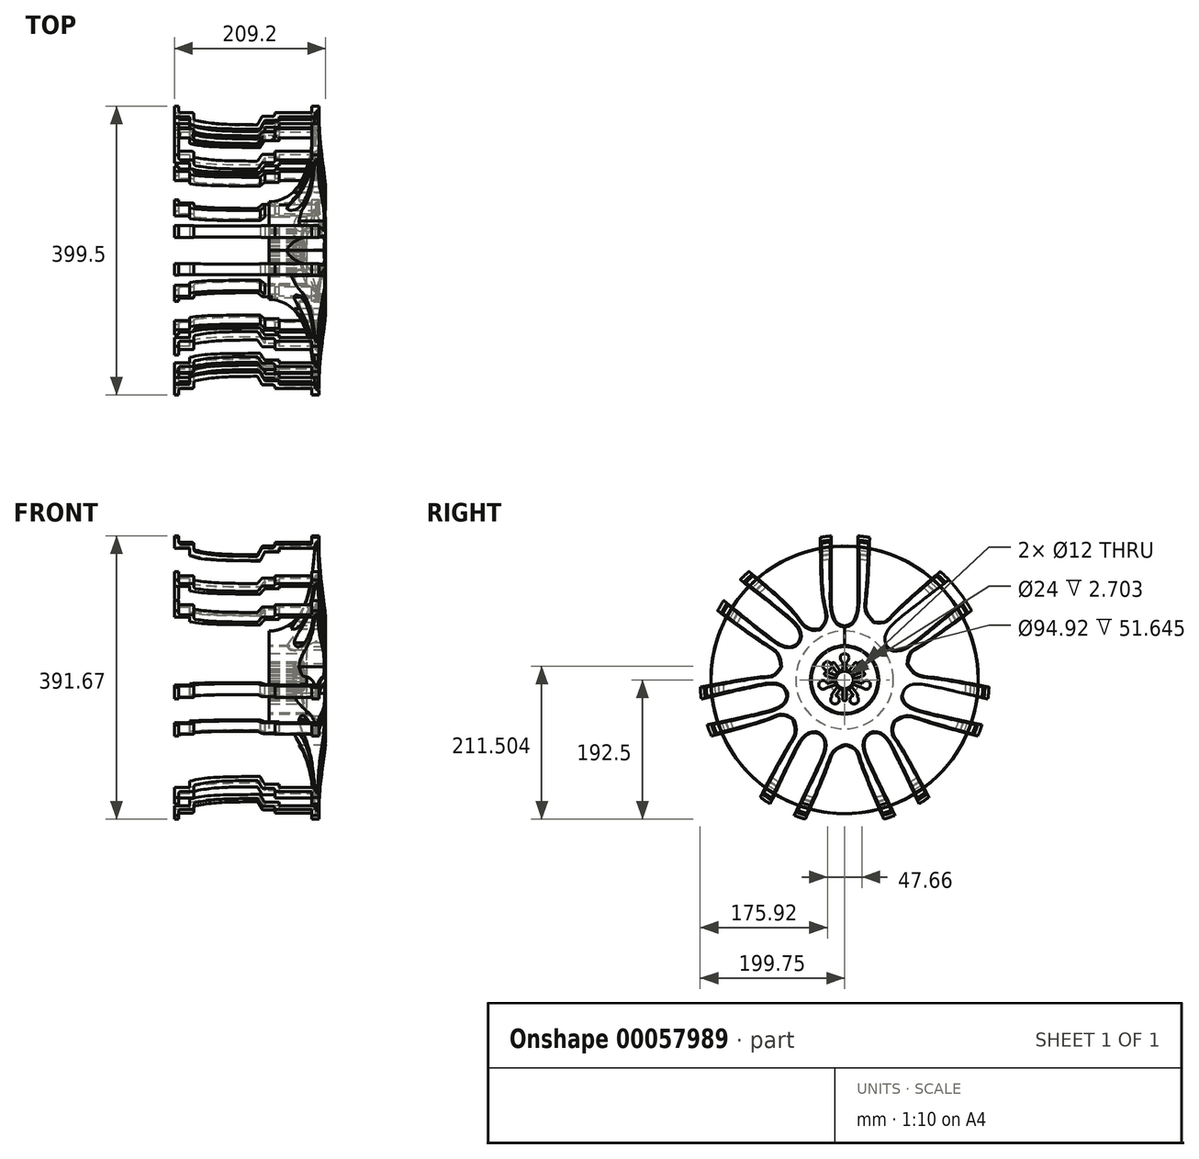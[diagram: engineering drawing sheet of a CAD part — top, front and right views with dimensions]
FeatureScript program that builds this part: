
annotation { "Feature Type Name" : "Feature", "Feature Type Description" : "" }
export const myFeature = defineFeature(function(context is Context, id is Id, definition is map)
    precondition{}
    {
        {
            var Q0;
            Q0=qCreatedBy(makeId("Front.planeOp"),FACE);
            var sketch = newSketch(context, id + "F0", { "sketchPlane" : qUnion([Q0])});
            skLineSegment(sketch, "E0", {"start": v(-200, 200) * mm, "end": v(0, 200) * mm, "construction": true});
            skLineSegment(sketch, "E1", {"start": v(0, 200) * mm, "end": v(0, 0) * mm, "construction": true});
            skLineSegment(sketch, "E2", {"start": v(0, 0) * mm, "end": v(-200, 0) * mm, "construction": true});
            skLineSegment(sketch, "E3", {"start": v(-200, 0) * mm, "end": v(-200, 200) * mm, "construction": true});
            skLineSegment(sketch, "E4", {"start": v(-200, 168) * mm, "end": v(0, 168) * mm, "construction": true});
            skLineSegment(sketch, "E5", {"start": v(0, 200) * mm, "end": v(0, 185) * mm});
            skLineSegment(sketch, "E6", {"start": v(0, 185) * mm, "end": v(-55, 185) * mm});
            skLineSegment(sketch, "E7", {"start": v(-55, 185) * mm, "end": v(-55, 180) * mm});
            skLineSegment(sketch, "E8", {"start": v(-55, 180) * mm, "end": v(-75, 180) * mm});
            skLineSegment(sketch, "E9", {"start": v(-200, 200) * mm, "end": v(-200, 185) * mm});
            skLineSegment(sketch, "E10", {"start": v(-200, 185) * mm, "end": v(-178.8, 185) * mm});
            skLineSegment(sketch, "E11", {"start": v(-178.8, 185) * mm, "end": v(-178.8, 175) * mm});
            skLineSegment(sketch, "E12", {"start": v(-75, 180) * mm, "end": v(-81.33, 168) * mm});
            skFitSpline(sketch, "E13", {"points": [v(-178.8, 175) * mm, v(-81.33, 168) * mm], "startDerivative": vector(39.43, -8.88) * mm, "endDerivative": vector(260.91, 0) * mm});
            skLineSegment(sketch, "E14", {"start": v(-200, 200) * mm, "end": v(-194, 200) * mm});
            skLineSegment(sketch, "E15", {"start": v(-194, 200) * mm, "end": v(-194, 191) * mm});
            skLineSegment(sketch, "E16", {"start": v(-194, 191) * mm, "end": v(-172.81, 191) * mm});
            skLineSegment(sketch, "E17", {"start": v(0, 200) * mm, "end": v(-10, 200) * mm});
            skLineSegment(sketch, "E18", {"start": v(-10, 200) * mm, "end": v(-10, 191) * mm});
            skLineSegment(sketch, "E19", {"start": v(-10, 191) * mm, "end": v(-61, 191) * mm});
            skLineSegment(sketch, "E20", {"start": v(-61, 191) * mm, "end": v(-61, 186) * mm});
            skLineSegment(sketch, "E21", {"start": v(-61, 186) * mm, "end": v(-78.62, 186) * mm});
            skLineSegment(sketch, "E22", {"start": v(-78.62, 186) * mm, "end": v(-84.94, 174) * mm});
            skLineSegment(sketch, "E23", {"start": v(-172.81, 191) * mm, "end": v(-172.81, 181) * mm});
            skFitSpline(sketch, "E24", {"points": [v(-172.81, 181) * mm, v(-84.94, 174) * mm], "startDerivative": vector(84.8, -22.47) * mm, "endDerivative": vector(95.11, -2) * mm});
            skSolve(sketch);
        }
        {
            var Q0;
            Q0=qSketchRegion(id+"F0",true);
            var Q1;
            Q1=sQuery(id+"F0.wireOp",EDGE,"E2");
            revolve(context, id + "F1", {"entities" : qUnion([Q0]), "axis" : qUnion([Q1]), "revolveType" : RevolveType.FULL});
        }
        {
            var Q0;
            Q0=makeQuery(id+"F1.opRevolve","SWEPT_EDGE",EDGE,{"disambiguationData":[OSD([sQuery(id+"F0.wireOp",EDGE,"E16"),sQuery(id+"F0.wireOp",EDGE,"E23")])]});
            fillet(context, id + "F2", {"entities" : qUnion([Q0]), "radius" : 3 * mm, "tangentPropagation" : true, "allowEdgeOverflow" : false});
        }
        {
            var Q0;
            Q0=makeQuery(id+"F1.opRevolve","SWEPT_EDGE",EDGE,{"disambiguationData":[OSD([sQuery(id+"F0.wireOp",EDGE,"E15"),sQuery(id+"F0.wireOp",EDGE,"E16")])]});
            fillet(context, id + "F3", {"entities" : qUnion([Q0]), "radius" : 3 * mm, "tangentPropagation" : true, "allowEdgeOverflow" : false});
        }
        {
            var Q0;
            Q0=makeQuery(id+"F1.opRevolve","SWEPT_EDGE",EDGE,{"disambiguationData":[OSD([sQuery(id+"F0.wireOp",EDGE,"E23"),sQuery(id+"F0.wireOp",EDGE,"E24")])]});
            fillet(context, id + "F4", {"entities" : qUnion([Q0]), "radius" : 3 * mm, "tangentPropagation" : true, "allowEdgeOverflow" : false});
        }
        {
            var Q0;
            Q0=makeQuery(id+"F1.opRevolve","SWEPT_EDGE",EDGE,{"disambiguationData":[OSD([sQuery(id+"F0.wireOp",EDGE,"E22"),sQuery(id+"F0.wireOp",EDGE,"E24")])]});
            fillet(context, id + "F5", {"entities" : qUnion([Q0]), "radius" : 3 * mm, "tangentPropagation" : true, "allowEdgeOverflow" : false});
        }
        {
            var Q0;
            Q0=makeQuery(id+"F1.opRevolve","SWEPT_EDGE",EDGE,{"disambiguationData":[OSD([sQuery(id+"F0.wireOp",EDGE,"E21"),sQuery(id+"F0.wireOp",EDGE,"E22")])]});
            fillet(context, id + "F6", {"entities" : qUnion([Q0]), "radius" : 3 * mm, "tangentPropagation" : true, "allowEdgeOverflow" : false});
        }
        {
            var Q0;
            Q0=makeQuery(id+"F1.opRevolve","SWEPT_EDGE",EDGE,{"disambiguationData":[OSD([sQuery(id+"F0.wireOp",EDGE,"E20"),sQuery(id+"F0.wireOp",EDGE,"E21")])]});
            fillet(context, id + "F7", {"entities" : qUnion([Q0]), "radius" : 3 * mm, "tangentPropagation" : true, "allowEdgeOverflow" : false});
        }
        {
            var Q0;
            Q0=makeQuery(id+"F1.opRevolve","SWEPT_FACE",FACE,{"disambiguationData":[OSD([sQuery(id+"F0.wireOp",EDGE,"E5")])]});
            var sketch = newSketch(context, id + "F8", { "sketchPlane" : qUnion([Q0])});
            skArc(sketch, "E25", {"start": v(82.65, 71.65) * mm, "mid": v(-145.3, -223.22) * mm, "end": v(182.84, -46.5) * mm});
            skArc(sketch, "E26", {"start": v(179.13, -35.13) * mm, "mid": v(109.4, 55.97) * mm, "end": v(0, 90.5) * mm});
            skLineSegment(sketch, "E27", {"start": v(179.13, -35.13) * mm, "end": v(122.22, 138.87) * mm});
            skArc(sketch, "E28.MirrorCS", {"start": v(80.26, 66.69) * mm, "mid": v(87.85, 62.8) * mm, "end": v(95.26, 58.59) * mm});
            skLineSegment(sketch, "E29.MirrorCS", {"start": v(95.26, 58.59) * mm, "end": v(106.47, 62.77) * mm});
            skArc(sketch, "E30.MirrorCS", {"start": v(106.47, 62.77) * mm, "mid": v(130.91, 43.85) * mm, "end": v(152.05, 21.3) * mm});
            skArc(sketch, "E31.1.0", {"start": v(60.97, 80.5) * mm, "mid": v(-53.73, 82.77) * mm, "end": v(-148.95, 18.78) * mm});
            skLineSegment(sketch, "E31.1.1", {"start": v(60.97, 80.5) * mm, "end": v(-110.55, 144.5) * mm});
            skArc(sketch, "E31.1.2", {"start": v(-82.67, 71.64) * mm, "mid": v(5.75, -290.42) * mm, "end": v(72.17, 76.3) * mm});
            skArc(sketch, "E31.1.3", {"start": v(-80.28, 66.67) * mm, "mid": v(-72.52, 70.2) * mm, "end": v(-64.6, 73.36) * mm});
            skArc(sketch, "E31.1.4", {"start": v(-60.88, 84.73) * mm, "mid": v(-30.84, 92.04) * mm, "end": v(-0.03, 94.5) * mm});
            skLineSegment(sketch, "E31.1.5", {"start": v(-64.6, 73.36) * mm, "end": v(-60.88, 84.73) * mm});
            skArc(sketch, "E31.2.0", {"start": v(-103.1, 60.2) * mm, "mid": v(-176.4, -28.05) * mm, "end": v(-185.73, -142.4) * mm});
            skLineSegment(sketch, "E31.2.1", {"start": v(-103.1, 60.2) * mm, "end": v(-260.08, -34) * mm});
            skArc(sketch, "E31.2.2", {"start": v(-185.74, -57.62) * mm, "mid": v(152.46, -214.24) * mm, "end": v(-92.84, 66.35) * mm});
            skArc(sketch, "E31.2.3", {"start": v(-180.36, -58.85) * mm, "mid": v(-178.28, -50.58) * mm, "end": v(-175.8, -42.42) * mm});
            skArc(sketch, "E31.2.4", {"start": v(-182.38, -32.42) * mm, "mid": v(-169.37, -4.38) * mm, "end": v(-152.08, 21.25) * mm});
            skLineSegment(sketch, "E31.2.5", {"start": v(-175.8, -42.42) * mm, "end": v(-182.38, -32.42) * mm});
            skArc(sketch, "E31.3.0", {"start": v(-189.53, -80.72) * mm, "mid": v(-166.24, -193.06) * mm, "end": v(-82.66, -271.64) * mm});
            skLineSegment(sketch, "E31.3.1", {"start": v(-189.53, -80.72) * mm, "end": v(-213.76, -262.19) * mm});
            skArc(sketch, "E31.3.2", {"start": v(-148.94, -218.8) * mm, "mid": v(184.37, -52.03) * mm, "end": v(-187.95, -68.87) * mm});
            skArc(sketch, "E31.3.3", {"start": v(-144.63, -215.36) * mm, "mid": v(-149.8, -208.57) * mm, "end": v(-154.64, -201.55) * mm});
            skArc(sketch, "E31.3.4", {"start": v(-166.55, -200.46) * mm, "mid": v(-180.36, -172.8) * mm, "end": v(-189.62, -143.3) * mm});
            skLineSegment(sketch, "E31.3.5", {"start": v(-154.64, -201.55) * mm, "end": v(-166.55, -200.46) * mm});
            skArc(sketch, "E31.4.0", {"start": v(-133.24, -236.16) * mm, "mid": v(-30.9, -287.99) * mm, "end": v(82.66, -271.64) * mm});
            skLineSegment(sketch, "E31.4.1", {"start": v(-133.24, -236.16) * mm, "end": v(-6.48, -368.25) * mm});
            skArc(sketch, "E31.4.2", {"start": v(0.01, -290.5) * mm, "mid": v(77.45, 74.06) * mm, "end": v(-141.52, -227.53) * mm});
            skArc(sketch, "E31.4.3", {"start": v(0.01, -285) * mm, "mid": v(-8.51, -284.8) * mm, "end": v(-17.02, -284.22) * mm});
            skArc(sketch, "E31.4.4", {"start": v(-25.3, -292.85) * mm, "mid": v(-55.53, -286.4) * mm, "end": v(-84.36, -275.25) * mm});
            skLineSegment(sketch, "E31.4.5", {"start": v(-17.02, -284.22) * mm, "end": v(-25.3, -292.85) * mm});
            skArc(sketch, "E31.5.0", {"start": v(23.38, -289.07) * mm, "mid": v(127.71, -241.36) * mm, "end": v(185.73, -142.4) * mm});
            skLineSegment(sketch, "E31.5.1", {"start": v(23.38, -289.07) * mm, "end": v(205.69, -272.31) * mm});
            skArc(sketch, "E31.5.2", {"start": v(148.95, -218.77) * mm, "mid": v(-87.8, 69.07) * mm, "end": v(11.47, -290.16) * mm});
            skArc(sketch, "E31.5.3", {"start": v(144.65, -215.33) * mm, "mid": v(139.18, -221.88) * mm, "end": v(133.41, -228.16) * mm});
            skArc(sketch, "E31.5.4", {"start": v(135, -240.02) * mm, "mid": v(111.11, -259.64) * mm, "end": v(84.42, -275.23) * mm});
            skLineSegment(sketch, "E31.5.5", {"start": v(133.41, -228.16) * mm, "end": v(135, -240.02) * mm});
            skArc(sketch, "E31.6.0", {"start": v(162.4, -199.6) * mm, "mid": v(190.15, -88.29) * mm, "end": v(148.95, 18.78) * mm});
            skLineSegment(sketch, "E31.6.1", {"start": v(162.4, -199.6) * mm, "end": v(262.97, -46.62) * mm});
            skArc(sketch, "E31.6.2", {"start": v(185.73, -57.6) * mm, "mid": v(-186.93, -63.23) * mm, "end": v(155.83, -209.6) * mm});
            skArc(sketch, "E31.6.3", {"start": v(180.36, -58.82) * mm, "mid": v(182.06, -67.18) * mm, "end": v(183.38, -75.6) * mm});
            skArc(sketch, "E31.6.4", {"start": v(193.64, -81.75) * mm, "mid": v(194.09, -112.66) * mm, "end": v(189.63, -143.25) * mm});
            skLineSegment(sketch, "E31.6.5", {"start": v(183.38, -75.6) * mm, "end": v(193.64, -81.75) * mm});
            skSolve(sketch);
        }
        {
            var Q0;
            {var subQ0=sQuery(id+"F0.wireOp",EDGE,"E5");Q0=makeQuery(id+"F8.imprint","IMPRINT",FACE,{"disambiguationData":[TD([[makeQuery(id+"F8.imprint","IMPRINT",EDGE,{"derivedFrom":makeQuery(id+"F1.opRevolve","SWEPT_EDGE",EDGE,{"disambiguationData":[OSD([subQ0,sQuery(id+"F0.wireOp",EDGE,"E17")])]})}),1.0]])]});}
            cPlane(context, id + "F9", {"entities" : qUnion([Q0]), "cplaneType" : CPlaneType.OFFSET, "offset" : 2 * mm, "width" : 152.4 * mm, "height" : 152.4 * mm});
        }
        {
            var Q0;
            Q0=qCreatedBy(id+"F9.planeOp",FACE);
            var sketch = newSketch(context, id + "F10", { "sketchPlane" : qUnion([Q0])});
            skArc(sketch, "E32", {"start": v(-193.59, 18.53) * mm, "mid": v(-189.67, -43.35) * mm, "end": v(-166.47, -100.86) * mm});
            skArc(sketch, "E33", {"start": v(175.53, 57.28) * mm, "mid": v(144.15, 115.24) * mm, "end": v(94.42, 158.5) * mm});
            skLineSegment(sketch, "E34", {"start": v(-182.24, 67.68) * mm, "end": v(-175.61, 57.03) * mm});
            skLineSegment(sketch, "E35", {"start": v(-106.28, 162.62) * mm, "end": v(-94.48, 158.46) * mm});
            skLineSegment(sketch, "E36", {"start": v(-65.52, 172.44) * mm, "end": v(-61.02, 184.4) * mm});
            skLineSegment(sketch, "E37", {"start": v(-193.59, 18.53) * mm, "end": v(-183.05, 24.59) * mm});
            skLineSegment(sketch, "E38", {"start": v(-166.47, -100.86) * mm, "end": v(-153.9, -102.44) * mm});
            skLineSegment(sketch, "E39", {"start": v(-135.3, -140) * mm, "end": v(-133.44, -128.02) * mm});
            skLineSegment(sketch, "E40", {"start": v(-25.44, -193.1) * mm, "end": v(-16.16, -184.3) * mm});
            skLineSegment(sketch, "E41", {"start": v(25.42, -193.1) * mm, "end": v(16.48, -184.26) * mm});
            skLineSegment(sketch, "E42", {"start": v(134.96, -140.33) * mm, "end": v(132.99, -128.48) * mm});
            skLineSegment(sketch, "E43", {"start": v(166.75, -100.4) * mm, "end": v(154, -102.28) * mm});
            skLineSegment(sketch, "E44", {"start": v(193.66, 17.73) * mm, "end": v(183.08, 24.35) * mm});
            skLineSegment(sketch, "E45", {"start": v(175.53, 57.28) * mm, "end": v(182.24, 67.7) * mm});
            skLineSegment(sketch, "E46", {"start": v(64.54, 172.8) * mm, "end": v(60.48, 184.58) * mm});
            skLineSegment(sketch, "E47", {"start": v(94.42, 158.5) * mm, "end": v(106.43, 162.52) * mm});
            skArc(sketch, "E48.trimOffspring", {"start": v(-106.28, 162.62) * mm, "mid": v(-151.87, 121.24) * mm, "end": v(-182.24, 67.68) * mm});
            skArc(sketch, "E49.trimOffspring", {"start": v(60.48, 184.58) * mm, "mid": v(-0.28, 194.23) * mm, "end": v(-61.02, 184.4) * mm});
            skArc(sketch, "E50.trimOffspring", {"start": v(-135.3, -140) * mm, "mid": v(-84.64, -175.4) * mm, "end": v(-25.44, -193.1) * mm});
            skArc(sketch, "E51.trimOffspring", {"start": v(25.42, -193.1) * mm, "mid": v(84.42, -175.5) * mm, "end": v(134.96, -140.33) * mm});
            skArc(sketch, "E52.trimOffspring", {"start": v(166.75, -100.4) * mm, "mid": v(189.64, -43.48) * mm, "end": v(193.66, 17.73) * mm});
            skArc(sketch, "E53.trimOffspring", {"start": v(182.24, 67.7) * mm, "mid": v(151.92, 121.17) * mm, "end": v(106.43, 162.52) * mm});
            skArc(sketch, "E54.trimOffspring", {"start": v(154, -102.28) * mm, "mid": v(180.04, -41.6) * mm, "end": v(183.08, 24.35) * mm});
            skArc(sketch, "E55.trimOffspring", {"start": v(16.48, -184.26) * mm, "mid": v(79.77, -166.89) * mm, "end": v(132.99, -128.48) * mm});
            skArc(sketch, "E56.trimOffspring", {"start": v(-133.44, -128.02) * mm, "mid": v(-79.92, -166.82) * mm, "end": v(-16.16, -184.3) * mm});
            skArc(sketch, "E57.trimOffspring", {"start": v(-183.05, 24.59) * mm, "mid": v(-180.05, -41.58) * mm, "end": v(-153.9, -102.44) * mm});
            skArc(sketch, "E58.trimOffspring", {"start": v(-94.48, 158.46) * mm, "mid": v(-144.25, 115.12) * mm, "end": v(-175.61, 57.03) * mm});
            skArc(sketch, "E59.trimOffspring", {"start": v(64.54, 172.8) * mm, "mid": v(-0.52, 184.45) * mm, "end": v(-65.52, 172.44) * mm});
            skSolve(sketch);
        }
        {
            var Q0;
            Q0=qSketchRegion(id+"F10",true);
            extrude(context, id + "F11", {"entities" : qUnion([Q0]), "operationType" : NewBodyOperationType.REMOVE, "oppositeDirection" : true, "depth" : 4 * mm});
        }
        {
            var Q0;
            Q0=qCreatedBy(makeId("Front.planeOp"),FACE);
            var sketch = newSketch(context, id + "F12", { "sketchPlane" : qUnion([Q0])});
            skLineSegment(sketch, "E60", {"start": v(0, 191.75) * mm, "end": v(-4.92, 191.75) * mm});
            skLineSegment(sketch, "E61", {"start": v(-17.14, 47.46) * mm, "end": v(-68.78, 47.46) * mm});
            skLineSegment(sketch, "E62", {"start": v(-68.78, 47.46) * mm, "end": v(-68.78, 67.56) * mm});
            skFitSpline(sketch, "E63", {"points": [v(0, 191.75) * mm, v(-17.14, 47.46) * mm], "startDerivative": vector(0, -276.55) * mm, "endDerivative": vector(-139.92, -42.5) * mm});
            skFitSpline(sketch, "E64", {"points": [v(-4.92, 191.75) * mm, v(-68.78, 67.56) * mm], "startDerivative": vector(-14.16, -151.7) * mm, "endDerivative": vector(-167.36, -6.57) * mm});
            skLineSegment(sketch, "E65", {"start": v(-115.73, 0) * mm, "end": v(0, 0) * mm, "construction": true});
            skSolve(sketch);
        }
        {
            var Q0;
            Q0=qCreatedBy(makeId("Front.planeOp"),FACE);
            var sketch = newSketch(context, id + "F13", { "sketchPlane" : qUnion([Q0])});
            skLineSegment(sketch, "E66", {"start": v(0, 0) * mm, "end": v(181.72, 0) * mm, "construction": true});
            skSolve(sketch);
        }
        {
            var Q0;
            Q0=qSketchRegion(id+"F12",true);
            var Q1;
            Q1=sQuery(id+"F12.wireOp",EDGE,"E65");
            revolve(context, id + "F14", {"entities" : qUnion([Q0]), "axis" : qUnion([Q1]), "revolveType" : RevolveType.FULL});
        }
        {
            var Q0;
            Q0=qCreatedBy(makeId("Right.planeOp"),FACE);
            var sketch = newSketch(context, id + "F15", { "sketchPlane" : qUnion([Q0])});
            skFitSpline(sketch, "E67", {"points": [v(18.15, 199.17) * mm, v(18.5, 120.67) * mm, v(0, 74.57) * mm], "startDerivative": vector(4.65, -291.73) * mm, "endDerivative": vector(-131.17, -9.85) * mm});
            skFitSpline(sketch, "E68", {"points": [v(34.66, 196.97) * mm, v(29.92, 109.84) * mm, v(40.85, 80.56) * mm], "startDerivative": vector(-3.25, -176.46) * mm, "endDerivative": vector(105.11, -100.34) * mm});
            skLineSegment(sketch, "E69", {"start": v(0, 200) * mm, "end": v(0, 74.57) * mm});
            skFitSpline(sketch, "E70.MirrorCS", {"points": [v(-18.15, 199.17) * mm, v(-18.5, 120.67) * mm, v(0, 74.57) * mm], "startDerivative": vector(-4.65, -291.73) * mm, "endDerivative": vector(131.17, -9.85) * mm});
            skFitSpline(sketch, "E71.MirrorCS", {"points": [v(-33.77, 197.13) * mm, v(-29, 105.47) * mm, v(-34.74, 70.51) * mm], "startDerivative": vector(4.34, -176.59) * mm, "endDerivative": vector(-104.67, -100.89) * mm});
            skLineSegment(sketch, "E72.1.0", {"start": v(-156.37, 124.7) * mm, "end": v(-58.3, 46.5) * mm, "construction": true});
            skLineSegment(sketch, "E72.3.0", {"start": v(-86.78, -180.2) * mm, "end": v(-32.36, -67.19) * mm, "construction": true});
            skLineSegment(sketch, "E72.4.0", {"start": v(86.78, -180.2) * mm, "end": v(32.36, -67.19) * mm, "construction": true});
            skLineSegment(sketch, "E72.5.0", {"start": v(194.99, -44.5) * mm, "end": v(72.7, -16.6) * mm, "construction": true});
            skLineSegment(sketch, "E72.6.0", {"start": v(156.37, 124.7) * mm, "end": v(58.3, 46.5) * mm, "construction": true});
            skPoint(sketch, "E72.center", {"position": v(0, 0) * mm});
            skFitSpline(sketch, "E73.MirrorCS", {"points": [v(-132.4, 149.9) * mm, v(-65.2, 87.81) * mm, v(-34.74, 70.51) * mm], "startDerivative": vector(138.32, -110.16) * mm, "endDerivative": vector(143.74, 22.07) * mm});
            skFitSpline(sketch, "E74.MirrorCS", {"points": [v(198.24, -26.48) * mm, v(121.76, -8.8) * mm, v(80.37, -18.34) * mm], "startDerivative": vector(-283.38, 69.45) * mm, "endDerivative": vector(-38.79, -125.69) * mm});
            skFitSpline(sketch, "E75.MirrorCS", {"points": [v(198.24, -26.48) * mm, v(121.76, -8.8) * mm, v(80.37, -18.34) * mm], "startDerivative": vector(-283.38, 69.45) * mm, "endDerivative": vector(-38.79, -125.69) * mm});
            skFitSpline(sketch, "E76.MirrorCS", {"points": [v(190.1, -62.15) * mm, v(113.53, -44.9) * mm, v(80.37, -18.34) * mm], "startDerivative": vector(-285.45, 60.38) * mm, "endDerivative": vector(19.59, 130.07) * mm});
            skFitSpline(sketch, "E77.MirrorCS", {"points": [v(132.4, 149.9) * mm, v(64.99, 88.84) * mm, v(40.85, 80.56) * mm], "startDerivative": vector(-133.89, -115.5) * mm, "endDerivative": vector(-144.5, 16.42) * mm});
            skFitSpline(sketch, "E78", {"points": [v(144.18, 138.35) * mm, v(81.98, 90.08) * mm, v(58.3, 46.5) * mm], "startDerivative": vector(-155.93, -120.73) * mm, "endDerivative": vector(65.65, -114.26) * mm});
            skFitSpline(sketch, "E79.MirrorCS", {"points": [v(166.97, 109.78) * mm, v(106.06, 59.88) * mm, v(58.3, 46.5) * mm], "startDerivative": vector(-152.4, -125.16) * mm, "endDerivative": vector(-96.79, 89.43) * mm});
            skFitSpline(sketch, "E80.MirrorCS", {"points": [v(175.6, 95.71) * mm, v(101.08, 43.59) * mm, v(87.63, 21.9) * mm], "startDerivative": vector(-142.4, -104.83) * mm, "endDerivative": vector(-16.14, -144.53) * mm});
            skFitSpline(sketch, "E81.MirrorCS", {"points": [v(199.75, -10.04) * mm, v(113.75, 4.73) * mm, v(87.63, 21.9) * mm], "startDerivative": vector(-172.76, 36.1) * mm, "endDerivative": vector(-74.43, 124.8) * mm});
            skFitSpline(sketch, "E82.MirrorCS", {"points": [v(184.32, -77.62) * mm, v(100.43, -53.62) * mm, v(69.45, -57.75) * mm], "startDerivative": vector(-171.31, 42.43) * mm, "endDerivative": vector(-121.21, -80.15) * mm});
            skFitSpline(sketch, "E83.MirrorCS", {"points": [v(116.69, -162.43) * mm, v(72.16, -83.13) * mm, v(69.45, -57.75) * mm], "startDerivative": vector(-82.8, 156.23) * mm, "endDerivative": vector(48.16, 137.22) * mm});
            skFitSpline(sketch, "E84.MirrorCS", {"points": [v(102.9, -171.5) * mm, v(69.03, -100.69) * mm, v(35.77, -74.28) * mm], "startDerivative": vector(-122.38, 264.86) * mm, "endDerivative": vector(-122.45, -48.04) * mm});
            skFitSpline(sketch, "E85.MirrorCS", {"points": [v(69.93, -187.38) * mm, v(35.68, -116.75) * mm, v(35.77, -74.28) * mm], "startDerivative": vector(-130.77, 260.82) * mm, "endDerivative": vector(113.9, 65.78) * mm});
            skFitSpline(sketch, "E86.MirrorCS", {"points": [v(54.24, -192.5) * mm, v(20, -108.24) * mm, v(1.85, -90.3) * mm], "startDerivative": vector(-70.52, 162.15) * mm, "endDerivative": vector(-137.31, 47.9) * mm});
            skFitSpline(sketch, "E87.MirrorCS", {"points": [v(-54.24, -192.5) * mm, v(-20.7, -111.95) * mm, v(1.85, -90.3) * mm], "startDerivative": vector(73.64, 160.4) * mm, "endDerivative": vector(138.24, 44.8) * mm});
            skFitSpline(sketch, "E88.MirrorCS", {"points": [v(-69.93, -187.38) * mm, v(-35.68, -116.75) * mm, v(-35.77, -74.28) * mm], "startDerivative": vector(130.77, 260.82) * mm, "endDerivative": vector(-113.9, 65.78) * mm});
            skFitSpline(sketch, "E89.MirrorCS", {"points": [v(-102.9, -171.5) * mm, v(-69.03, -100.69) * mm, v(-35.77, -74.28) * mm], "startDerivative": vector(122.38, 264.86) * mm, "endDerivative": vector(122.45, -48.04) * mm});
            skFitSpline(sketch, "E90.MirrorCS", {"points": [v(-116.69, -162.43) * mm, v(-74.62, -85.98) * mm, v(-71.75, -54.86) * mm], "startDerivative": vector(79.49, 157.58) * mm, "endDerivative": vector(-51.17, 136) * mm});
            skFitSpline(sketch, "E91.MirrorCS", {"points": [v(-184.32, -77.62) * mm, v(-97.1, -51.85) * mm, v(-71.75, -54.86) * mm], "startDerivative": vector(170.74, 45.97) * mm, "endDerivative": vector(123.06, -77.49) * mm});
            skFitSpline(sketch, "E92.MirrorCS", {"points": [v(-190.1, -62.15) * mm, v(-113.53, -44.9) * mm, v(-80.37, -18.34) * mm], "startDerivative": vector(285.45, 60.38) * mm, "endDerivative": vector(-19.59, 130.07) * mm});
            skFitSpline(sketch, "E93.MirrorCS", {"points": [v(-198.24, -26.48) * mm, v(-121.76, -8.8) * mm, v(-80.37, -18.34) * mm], "startDerivative": vector(283.38, 69.45) * mm, "endDerivative": vector(38.79, -125.69) * mm});
            skLineSegment(sketch, "E94.MirrorCS", {"start": v(-194.99, -44.5) * mm, "end": v(-72.7, -16.6) * mm, "construction": true});
            skFitSpline(sketch, "E95.MirrorCS", {"points": [v(-199.75, -10.04) * mm, v(-109.98, 4.58) * mm, v(-88.45, 18.3) * mm], "startDerivative": vector(173.78, 32.67) * mm, "endDerivative": vector(77.25, 123.2) * mm});
            skFitSpline(sketch, "E96.MirrorCS", {"points": [v(-175.6, 95.71) * mm, v(-104.53, 45.09) * mm, v(-88.45, 18.3) * mm], "startDerivative": vector(139.98, -107.48) * mm, "endDerivative": vector(12.9, -144.74) * mm});
            skFitSpline(sketch, "E97.MirrorCS", {"points": [v(-167.12, 109.87) * mm, v(-105.88, 60.77) * mm, v(-64.46, 51.4) * mm], "startDerivative": vector(225.18, -185.53) * mm, "endDerivative": vector(89.48, 96.41) * mm});
            skFitSpline(sketch, "E98.MirrorCS", {"points": [v(-144.3, 138.48) * mm, v(-82.8, 89.7) * mm, v(-64.46, 51.4) * mm], "startDerivative": vector(230.98, -178.25) * mm, "endDerivative": vector(-74.08, -108.69) * mm});
            skArc(sketch, "E99", {"start": v(-33.77, 197.13) * mm, "mid": v(-86.37, 180.39) * mm, "end": v(-132.4, 149.9) * mm});
            skArc(sketch, "E100.trimOffspring", {"start": v(18.15, 199.17) * mm, "mid": v(0, 200) * mm, "end": v(-18.15, 199.17) * mm});
            skArc(sketch, "E101.trimOffspring", {"start": v(199.75, -10.04) * mm, "mid": v(194.99, 44.5) * mm, "end": v(175.6, 95.71) * mm});
            skArc(sketch, "E102.trimOffspring", {"start": v(190.1, -62.15) * mm, "mid": v(194.99, -44.5) * mm, "end": v(198.24, -26.48) * mm});
            skArc(sketch, "E103.trimOffspring", {"start": v(116.69, -162.43) * mm, "mid": v(156.37, -124.7) * mm, "end": v(184.32, -77.62) * mm});
            skArc(sketch, "E104.trimOffspring", {"start": v(69.93, -187.38) * mm, "mid": v(86.78, -180.2) * mm, "end": v(102.9, -171.5) * mm});
            skArc(sketch, "E105.trimOffspring", {"start": v(-54.24, -192.5) * mm, "mid": v(0, -200) * mm, "end": v(54.24, -192.5) * mm});
            skArc(sketch, "E106.trimOffspring", {"start": v(-102.9, -171.5) * mm, "mid": v(-86.78, -180.2) * mm, "end": v(-69.93, -187.38) * mm});
            skArc(sketch, "E107.trimOffspring", {"start": v(-184.32, -77.62) * mm, "mid": v(-156.37, -124.7) * mm, "end": v(-116.69, -162.43) * mm});
            skArc(sketch, "E108.trimOffspring", {"start": v(-198.24, -26.48) * mm, "mid": v(-194.99, -44.5) * mm, "end": v(-190.1, -62.15) * mm});
            skArc(sketch, "E109.trimOffspring", {"start": v(-175.6, 95.71) * mm, "mid": v(-194.99, 44.5) * mm, "end": v(-199.75, -10.04) * mm});
            skArc(sketch, "E110.trimOffspring", {"start": v(-144.3, 138.48) * mm, "mid": v(-156.37, 124.7) * mm, "end": v(-167.12, 109.87) * mm});
            skArc(sketch, "E111.trimOffspring", {"start": v(132.4, 149.9) * mm, "mid": v(86.78, 180.2) * mm, "end": v(34.66, 196.97) * mm});
            skArc(sketch, "E112", {"start": v(144.18, 138.35) * mm, "mid": v(156.23, 124.59) * mm, "end": v(166.97, 109.78) * mm});
            skSolve(sketch);
        }
        {
            var Q0;
            Q0=qSketchRegion(id+"F15",true);
            extrude(context, id + "F16", {"entities" : qUnion([Q0]), "operationType" : NewBodyOperationType.REMOVE, "endBound" : BoundingType.THROUGH_ALL, "depth" : 25.4 * mm, "hasSecondDirection" : true, "secondDirectionBound" : SecondDirectionBoundingType.THROUGH_ALL, "secondDirectionOppositeDirection" : true, "secondDirectionDepth" : 25.4 * mm});
        }
        {
            var Q0;
            Q0=makeQuery(id+"F16.boolean.opBoolean","COPY",FACE,{"derivedFrom":makeQuery(id+"F16.opExtrude","SWEPT_FACE",FACE,{"disambiguationData":[OSD([sQuery(id+"F15.wireOp",EDGE,"E79.MirrorCS")])]})});
            var Q1;
            Q1=makeQuery(id+"F16.boolean.opBoolean","INTERSECT",EDGE,{"derivedFrom":[makeQuery(id+"F14.opRevolve","SWEPT_FACE",FACE,{"disambiguationData":[OSD([sQuery(id+"F12.wireOp",EDGE,"E63")])]}),makeQuery(id+"F16.opExtrude","SWEPT_FACE",FACE,{"disambiguationData":[OSD([sQuery(id+"F15.wireOp",EDGE,"E68")])]})]});
            var Q2;
            Q2=makeQuery(id+"F16.boolean.opBoolean","INTERSECT",EDGE,{"derivedFrom":[makeQuery(id+"F14.opRevolve","SWEPT_FACE",FACE,{"disambiguationData":[OSD([sQuery(id+"F12.wireOp",EDGE,"E63")])]}),makeQuery(id+"F16.opExtrude","SWEPT_FACE",FACE,{"disambiguationData":[OSD([sQuery(id+"F15.wireOp",EDGE,"E77.MirrorCS")])]})]});
            var Q3;
            Q3=makeQuery(id+"F16.boolean.opBoolean","INTERSECT",EDGE,{"derivedFrom":[makeQuery(id+"F14.opRevolve","SWEPT_FACE",FACE,{"disambiguationData":[OSD([sQuery(id+"F12.wireOp",EDGE,"E63")])]}),makeQuery(id+"F16.opExtrude","SWEPT_FACE",FACE,{"disambiguationData":[OSD([sQuery(id+"F15.wireOp",EDGE,"E67")])]})]});
            var Q4;
            Q4=makeQuery(id+"F16.boolean.opBoolean","INTERSECT",EDGE,{"derivedFrom":[makeQuery(id+"F14.opRevolve","SWEPT_FACE",FACE,{"disambiguationData":[OSD([sQuery(id+"F12.wireOp",EDGE,"E63")])]}),makeQuery(id+"F16.opExtrude","SWEPT_FACE",FACE,{"disambiguationData":[OSD([sQuery(id+"F15.wireOp",EDGE,"E70.MirrorCS")])]})]});
            var Q5;
            Q5=makeQuery(id+"F16.boolean.opBoolean","INTERSECT",EDGE,{"derivedFrom":[makeQuery(id+"F14.opRevolve","SWEPT_FACE",FACE,{"disambiguationData":[OSD([sQuery(id+"F12.wireOp",EDGE,"E63")])]}),makeQuery(id+"F16.opExtrude","SWEPT_FACE",FACE,{"disambiguationData":[OSD([sQuery(id+"F15.wireOp",EDGE,"E71.MirrorCS")])]})]});
            var Q6;
            Q6=makeQuery(id+"F16.boolean.opBoolean","INTERSECT",EDGE,{"derivedFrom":[makeQuery(id+"F14.opRevolve","SWEPT_FACE",FACE,{"disambiguationData":[OSD([sQuery(id+"F12.wireOp",EDGE,"E63")])]}),makeQuery(id+"F16.opExtrude","SWEPT_FACE",FACE,{"disambiguationData":[OSD([sQuery(id+"F15.wireOp",EDGE,"E73.MirrorCS")])]})]});
            var Q7;
            Q7=makeQuery(id+"F16.boolean.opBoolean","INTERSECT",EDGE,{"derivedFrom":[makeQuery(id+"F14.opRevolve","SWEPT_FACE",FACE,{"disambiguationData":[OSD([sQuery(id+"F12.wireOp",EDGE,"E63")])]}),makeQuery(id+"F16.opExtrude","SWEPT_FACE",FACE,{"disambiguationData":[OSD([sQuery(id+"F15.wireOp",EDGE,"E97.MirrorCS")])]})]});
            var Q8;
            Q8=makeQuery(id+"F16.boolean.opBoolean","INTERSECT",EDGE,{"derivedFrom":[makeQuery(id+"F14.opRevolve","SWEPT_FACE",FACE,{"disambiguationData":[OSD([sQuery(id+"F12.wireOp",EDGE,"E63")])]}),makeQuery(id+"F16.opExtrude","SWEPT_FACE",FACE,{"disambiguationData":[OSD([sQuery(id+"F15.wireOp",EDGE,"E98.MirrorCS")])]})]});
            var Q9;
            Q9=makeQuery(id+"F16.boolean.opBoolean","INTERSECT",EDGE,{"derivedFrom":[makeQuery(id+"F14.opRevolve","SWEPT_FACE",FACE,{"disambiguationData":[OSD([sQuery(id+"F12.wireOp",EDGE,"E63")])]}),makeQuery(id+"F16.opExtrude","SWEPT_FACE",FACE,{"disambiguationData":[OSD([sQuery(id+"F15.wireOp",EDGE,"E96.MirrorCS")])]})]});
            var Q10;
            Q10=makeQuery(id+"F16.boolean.opBoolean","INTERSECT",EDGE,{"derivedFrom":[makeQuery(id+"F14.opRevolve","SWEPT_FACE",FACE,{"disambiguationData":[OSD([sQuery(id+"F12.wireOp",EDGE,"E63")])]}),makeQuery(id+"F16.opExtrude","SWEPT_FACE",FACE,{"disambiguationData":[OSD([sQuery(id+"F15.wireOp",EDGE,"E95.MirrorCS")])]})]});
            var Q11;
            Q11=makeQuery(id+"F16.boolean.opBoolean","INTERSECT",EDGE,{"derivedFrom":[makeQuery(id+"F14.opRevolve","SWEPT_FACE",FACE,{"disambiguationData":[OSD([sQuery(id+"F12.wireOp",EDGE,"E63")])]}),makeQuery(id+"F16.opExtrude","SWEPT_FACE",FACE,{"disambiguationData":[OSD([sQuery(id+"F15.wireOp",EDGE,"E93.MirrorCS")])]})]});
            var Q12;
            Q12=makeQuery(id+"F16.boolean.opBoolean","INTERSECT",EDGE,{"derivedFrom":[makeQuery(id+"F14.opRevolve","SWEPT_FACE",FACE,{"disambiguationData":[OSD([sQuery(id+"F12.wireOp",EDGE,"E63")])]}),makeQuery(id+"F16.opExtrude","SWEPT_FACE",FACE,{"disambiguationData":[OSD([sQuery(id+"F15.wireOp",EDGE,"E92.MirrorCS")])]})]});
            var Q13;
            Q13=makeQuery(id+"F16.boolean.opBoolean","INTERSECT",EDGE,{"derivedFrom":[makeQuery(id+"F14.opRevolve","SWEPT_FACE",FACE,{"disambiguationData":[OSD([sQuery(id+"F12.wireOp",EDGE,"E63")])]}),makeQuery(id+"F16.opExtrude","SWEPT_FACE",FACE,{"disambiguationData":[OSD([sQuery(id+"F15.wireOp",EDGE,"E91.MirrorCS")])]})]});
            var Q14;
            Q14=makeQuery(id+"F16.boolean.opBoolean","INTERSECT",EDGE,{"derivedFrom":[makeQuery(id+"F14.opRevolve","SWEPT_FACE",FACE,{"disambiguationData":[OSD([sQuery(id+"F12.wireOp",EDGE,"E63")])]}),makeQuery(id+"F16.opExtrude","SWEPT_FACE",FACE,{"disambiguationData":[OSD([sQuery(id+"F15.wireOp",EDGE,"E90.MirrorCS")])]})]});
            var Q15;
            Q15=makeQuery(id+"F16.boolean.opBoolean","INTERSECT",EDGE,{"derivedFrom":[makeQuery(id+"F14.opRevolve","SWEPT_FACE",FACE,{"disambiguationData":[OSD([sQuery(id+"F12.wireOp",EDGE,"E63")])]}),makeQuery(id+"F16.opExtrude","SWEPT_FACE",FACE,{"disambiguationData":[OSD([sQuery(id+"F15.wireOp",EDGE,"E89.MirrorCS")])]})]});
            var Q16;
            Q16=makeQuery(id+"F16.boolean.opBoolean","INTERSECT",EDGE,{"derivedFrom":[makeQuery(id+"F14.opRevolve","SWEPT_FACE",FACE,{"disambiguationData":[OSD([sQuery(id+"F12.wireOp",EDGE,"E63")])]}),makeQuery(id+"F16.opExtrude","SWEPT_FACE",FACE,{"disambiguationData":[OSD([sQuery(id+"F15.wireOp",EDGE,"E88.MirrorCS")])]})]});
            var Q17;
            Q17=makeQuery(id+"F16.boolean.opBoolean","INTERSECT",EDGE,{"derivedFrom":[makeQuery(id+"F14.opRevolve","SWEPT_FACE",FACE,{"disambiguationData":[OSD([sQuery(id+"F12.wireOp",EDGE,"E63")])]}),makeQuery(id+"F16.opExtrude","SWEPT_FACE",FACE,{"disambiguationData":[OSD([sQuery(id+"F15.wireOp",EDGE,"E87.MirrorCS")])]})]});
            var Q18;
            Q18=makeQuery(id+"F16.boolean.opBoolean","INTERSECT",EDGE,{"derivedFrom":[makeQuery(id+"F14.opRevolve","SWEPT_FACE",FACE,{"disambiguationData":[OSD([sQuery(id+"F12.wireOp",EDGE,"E63")])]}),makeQuery(id+"F16.opExtrude","SWEPT_FACE",FACE,{"disambiguationData":[OSD([sQuery(id+"F15.wireOp",EDGE,"E86.MirrorCS")])]})]});
            var Q19;
            Q19=makeQuery(id+"F16.boolean.opBoolean","INTERSECT",EDGE,{"derivedFrom":[makeQuery(id+"F14.opRevolve","SWEPT_FACE",FACE,{"disambiguationData":[OSD([sQuery(id+"F12.wireOp",EDGE,"E63")])]}),makeQuery(id+"F16.opExtrude","SWEPT_FACE",FACE,{"disambiguationData":[OSD([sQuery(id+"F15.wireOp",EDGE,"E85.MirrorCS")])]})]});
            var Q20;
            Q20=makeQuery(id+"F16.boolean.opBoolean","INTERSECT",EDGE,{"derivedFrom":[makeQuery(id+"F14.opRevolve","SWEPT_FACE",FACE,{"disambiguationData":[OSD([sQuery(id+"F12.wireOp",EDGE,"E63")])]}),makeQuery(id+"F16.opExtrude","SWEPT_FACE",FACE,{"disambiguationData":[OSD([sQuery(id+"F15.wireOp",EDGE,"E84.MirrorCS")])]})]});
            var Q21;
            Q21=makeQuery(id+"F16.boolean.opBoolean","INTERSECT",EDGE,{"derivedFrom":[makeQuery(id+"F14.opRevolve","SWEPT_FACE",FACE,{"disambiguationData":[OSD([sQuery(id+"F12.wireOp",EDGE,"E63")])]}),makeQuery(id+"F16.opExtrude","SWEPT_FACE",FACE,{"disambiguationData":[OSD([sQuery(id+"F15.wireOp",EDGE,"E83.MirrorCS")])]})]});
            var Q22;
            Q22=makeQuery(id+"F16.boolean.opBoolean","INTERSECT",EDGE,{"derivedFrom":[makeQuery(id+"F14.opRevolve","SWEPT_FACE",FACE,{"disambiguationData":[OSD([sQuery(id+"F12.wireOp",EDGE,"E63")])]}),makeQuery(id+"F16.opExtrude","SWEPT_FACE",FACE,{"disambiguationData":[OSD([sQuery(id+"F15.wireOp",EDGE,"E82.MirrorCS")])]})]});
            var Q23;
            Q23=makeQuery(id+"F16.boolean.opBoolean","INTERSECT",EDGE,{"derivedFrom":[makeQuery(id+"F14.opRevolve","SWEPT_FACE",FACE,{"disambiguationData":[OSD([sQuery(id+"F12.wireOp",EDGE,"E63")])]}),makeQuery(id+"F16.opExtrude","SWEPT_FACE",FACE,{"disambiguationData":[OSD([sQuery(id+"F15.wireOp",EDGE,"E76.MirrorCS")])]})]});
            var Q24;
            Q24=makeQuery(id+"F16.boolean.opBoolean","INTERSECT",EDGE,{"derivedFrom":[makeQuery(id+"F14.opRevolve","SWEPT_FACE",FACE,{"disambiguationData":[OSD([sQuery(id+"F12.wireOp",EDGE,"E63")])]}),makeQuery(id+"F16.opExtrude","SWEPT_FACE",FACE,{"disambiguationData":[OSD([sQuery(id+"F15.wireOp",EDGE,"E75.MirrorCS")])]})]});
            var Q25;
            Q25=makeQuery(id+"F16.boolean.opBoolean","INTERSECT",EDGE,{"derivedFrom":[makeQuery(id+"F14.opRevolve","SWEPT_FACE",FACE,{"disambiguationData":[OSD([sQuery(id+"F12.wireOp",EDGE,"E63")])]}),makeQuery(id+"F16.opExtrude","SWEPT_FACE",FACE,{"disambiguationData":[OSD([sQuery(id+"F15.wireOp",EDGE,"E81.MirrorCS")])]})]});
            var Q26;
            Q26=makeQuery(id+"F16.boolean.opBoolean","INTERSECT",EDGE,{"derivedFrom":[makeQuery(id+"F14.opRevolve","SWEPT_FACE",FACE,{"disambiguationData":[OSD([sQuery(id+"F12.wireOp",EDGE,"E63")])]}),makeQuery(id+"F16.opExtrude","SWEPT_FACE",FACE,{"disambiguationData":[OSD([sQuery(id+"F15.wireOp",EDGE,"E80.MirrorCS")])]})]});
            fillet(context, id + "F17", {"entities" : qUnion([Q0, Q1, Q2, Q3, Q4, Q5, Q6, Q7, Q8, Q9, Q10, Q11, Q12, Q13, Q14, Q15, Q16, Q17, Q18, Q19, Q20, Q21, Q22, Q23, Q24, Q25, Q26]), "radius" : 1.5 * mm, "tangentPropagation" : true, "allowEdgeOverflow" : false});
        }
        {
            var Q0;
            Q0=qCreatedBy(makeId("Front.planeOp"),FACE);
            var sketch = newSketch(context, id + "F18", { "sketchPlane" : qUnion([Q0])});
            skLineSegment(sketch, "E113", {"start": v(-25.81, 0) * mm, "end": v(-68.42, 0) * mm});
            skLineSegment(sketch, "E114", {"start": v(-68.42, 0) * mm, "end": v(-68.42, 46) * mm});
            skLineSegment(sketch, "E115", {"start": v(-68.42, 46) * mm, "end": v(-17.06, 46) * mm});
            skFitSpline(sketch, "E116", {"points": [v(-17.06, 46) * mm, v(-25.81, 0) * mm], "startDerivative": vector(-22.92, -48.32) * mm, "endDerivative": vector(0.45, -42) * mm});
            skSolve(sketch);
        }
        {
            var Q0;
            Q0=qSketchRegion(id+"F18",true);
            var Q1;
            Q1=sQuery(id+"F13.wireOp",EDGE,"E66");
            revolve(context, id + "F19", {"entities" : qUnion([Q0]), "axis" : qUnion([Q1]), "revolveType" : RevolveType.FULL});
        }
        {
            var Q0;
            Q0=qCreatedBy(makeId("Front.planeOp"),FACE);
            var sketch = newSketch(context, id + "F20", { "sketchPlane" : qUnion([Q0])});
            skLineSegment(sketch, "E117", {"start": v(-35, 0) * mm, "end": v(-35, 20.92) * mm});
            skLineSegment(sketch, "E118", {"start": v(-35, 20.92) * mm, "end": v(-20.3, 14) * mm});
            skLineSegment(sketch, "E119", {"start": v(-20.3, 14) * mm, "end": v(-20.3, 12) * mm});
            skLineSegment(sketch, "E120", {"start": v(-20.3, 12) * mm, "end": v(-23, 12) * mm});
            skLineSegment(sketch, "E121", {"start": v(-23, 12) * mm, "end": v(-23, 0) * mm});
            skLineSegment(sketch, "E122", {"start": v(-23, 0) * mm, "end": v(-35, 0) * mm});
            skSolve(sketch);
        }
        {
            var Q0;
            Q0=qSketchRegion(id+"F20",true);
            var Q1;
            Q1=sQuery(id+"F20.wireOp",EDGE,"E122");
            revolve(context, id + "F21", {"entities" : qUnion([Q0]), "axis" : qUnion([Q1]), "revolveType" : RevolveType.FULL});
        }
        {
            var Q0;
            Q0=qCreatedBy(makeId("Right.planeOp"),FACE);
            var sketch = newSketch(context, id + "F22", { "sketchPlane" : qUnion([Q0])});
            skLineSegment(sketch, "E123", {"start": v(-2.57, 26.45) * mm, "end": v(-2.57, 16.29) * mm});
            skLineSegment(sketch, "E124", {"start": v(2.5, 25.87) * mm, "end": v(2.5, 15.7) * mm});
            skArc(sketch, "E125", {"start": v(-2.57, 26.45) * mm, "mid": v(0.3, 29) * mm, "end": v(2.5, 25.87) * mm});
            skArc(sketch, "E126", {"start": v(-2.57, 16.29) * mm, "mid": v(-0.3, 13.73) * mm, "end": v(2.5, 15.7) * mm});
            skLineSegment(sketch, "E127", {"start": v(0, 26.45) * mm, "end": v(0, 16.29) * mm});
            skLineSegment(sketch, "E128.1.0", {"start": v(-13.18, 22.4) * mm, "end": v(-7.2, 14.18) * mm});
            skLineSegment(sketch, "E128.1.1", {"start": v(-17.63, 19.89) * mm, "end": v(-11.66, 11.67) * mm});
            skArc(sketch, "E128.1.2", {"start": v(-17.63, 19.89) * mm, "mid": v(-16.81, 23.64) * mm, "end": v(-13.18, 22.4) * mm});
            skArc(sketch, "E128.1.3", {"start": v(-11.66, 11.67) * mm, "mid": v(-8.3, 10.94) * mm, "end": v(-7.2, 14.18) * mm});
            skLineSegment(sketch, "E128.2.0", {"start": v(-23.83, 10.38) * mm, "end": v(-14.16, 7.24) * mm});
            skLineSegment(sketch, "E128.2.1", {"start": v(-25.95, 5.73) * mm, "end": v(-16.29, 2.59) * mm});
            skArc(sketch, "E128.2.2", {"start": v(-25.95, 5.73) * mm, "mid": v(-27.5, 9.24) * mm, "end": v(-23.83, 10.38) * mm});
            skArc(sketch, "E128.2.3", {"start": v(-16.29, 2.59) * mm, "mid": v(-13.15, 3.97) * mm, "end": v(-14.16, 7.24) * mm});
            skLineSegment(sketch, "E128.3.0", {"start": v(-25.38, -5.6) * mm, "end": v(-15.71, -2.47) * mm});
            skLineSegment(sketch, "E128.3.1", {"start": v(-24.36, -10.62) * mm, "end": v(-14.7, -7.48) * mm});
            skArc(sketch, "E128.3.2", {"start": v(-24.36, -10.62) * mm, "mid": v(-27.68, -8.69) * mm, "end": v(-25.38, -5.6) * mm});
            skArc(sketch, "E128.3.3", {"start": v(-14.7, -7.48) * mm, "mid": v(-12.97, -4.52) * mm, "end": v(-15.71, -2.47) * mm});
            skLineSegment(sketch, "E128.4.0", {"start": v(-17.23, -19.45) * mm, "end": v(-11.26, -11.23) * mm});
            skLineSegment(sketch, "E128.4.1", {"start": v(-13.46, -22.91) * mm, "end": v(-7.5, -14.7) * mm});
            skArc(sketch, "E128.4.2", {"start": v(-13.46, -22.91) * mm, "mid": v(-17.29, -23.3) * mm, "end": v(-17.23, -19.45) * mm});
            skArc(sketch, "E128.4.3", {"start": v(-7.5, -14.7) * mm, "mid": v(-7.84, -11.28) * mm, "end": v(-11.26, -11.23) * mm});
            skLineSegment(sketch, "E128.5.0", {"start": v(-2.5, -25.87) * mm, "end": v(-2.5, -15.7) * mm});
            skLineSegment(sketch, "E128.5.1", {"start": v(2.57, -26.45) * mm, "end": v(2.57, -16.29) * mm});
            skArc(sketch, "E128.5.2", {"start": v(2.57, -26.45) * mm, "mid": v(-0.3, -29) * mm, "end": v(-2.5, -25.87) * mm});
            skArc(sketch, "E128.5.3", {"start": v(2.57, -16.29) * mm, "mid": v(0.3, -13.73) * mm, "end": v(-2.5, -15.7) * mm});
            skLineSegment(sketch, "E128.6.0", {"start": v(13.18, -22.4) * mm, "end": v(7.2, -14.18) * mm});
            skLineSegment(sketch, "E128.6.1", {"start": v(17.63, -19.89) * mm, "end": v(11.66, -11.67) * mm});
            skArc(sketch, "E128.6.2", {"start": v(17.63, -19.89) * mm, "mid": v(16.81, -23.64) * mm, "end": v(13.18, -22.4) * mm});
            skArc(sketch, "E128.6.3", {"start": v(11.66, -11.67) * mm, "mid": v(8.3, -10.94) * mm, "end": v(7.2, -14.18) * mm});
            skLineSegment(sketch, "E128.7.0", {"start": v(23.83, -10.38) * mm, "end": v(14.16, -7.24) * mm});
            skLineSegment(sketch, "E128.7.1", {"start": v(25.95, -5.73) * mm, "end": v(16.29, -2.59) * mm});
            skArc(sketch, "E128.7.2", {"start": v(25.95, -5.73) * mm, "mid": v(27.5, -9.24) * mm, "end": v(23.83, -10.38) * mm});
            skArc(sketch, "E128.7.3", {"start": v(16.29, -2.59) * mm, "mid": v(13.15, -3.97) * mm, "end": v(14.16, -7.24) * mm});
            skLineSegment(sketch, "E128.8.0", {"start": v(25.38, 5.6) * mm, "end": v(15.71, 2.47) * mm});
            skLineSegment(sketch, "E128.8.1", {"start": v(24.36, 10.62) * mm, "end": v(14.7, 7.48) * mm});
            skArc(sketch, "E128.8.2", {"start": v(24.36, 10.62) * mm, "mid": v(27.68, 8.69) * mm, "end": v(25.38, 5.6) * mm});
            skArc(sketch, "E128.8.3", {"start": v(14.7, 7.48) * mm, "mid": v(12.97, 4.52) * mm, "end": v(15.71, 2.47) * mm});
            skLineSegment(sketch, "E128.9.0", {"start": v(17.23, 19.45) * mm, "end": v(11.26, 11.23) * mm});
            skLineSegment(sketch, "E128.9.1", {"start": v(13.46, 22.91) * mm, "end": v(7.5, 14.7) * mm});
            skArc(sketch, "E128.9.2", {"start": v(13.46, 22.91) * mm, "mid": v(17.29, 23.3) * mm, "end": v(17.23, 19.45) * mm});
            skArc(sketch, "E128.9.3", {"start": v(7.5, 14.7) * mm, "mid": v(7.84, 11.28) * mm, "end": v(11.26, 11.23) * mm});
            skPoint(sketch, "E128.center", {"position": v(0, 0) * mm});
            skSolve(sketch);
        }
        {
            var Q0;
            Q0=qSketchRegion(id+"F22",true);
            extrude(context, id + "F23", {"entities" : qUnion([Q0]), "operationType" : NewBodyOperationType.REMOVE, "endBound" : BoundingType.THROUGH_ALL, "oppositeDirection" : true, "depth" : 24.13 * mm});
        }
        {
            var Q0;
            Q0=qCreatedBy(makeId("Right.planeOp"),FACE);
            var sketch = newSketch(context, id + "F24", { "sketchPlane" : qUnion([Q0])});
            skCircle(sketch, "E129", {"center": v(0, 30.48) * mm, "radius": 6 * mm});
            skCircle(sketch, "E130.1.0", {"center": v(-23.83, 19) * mm, "radius": 6 * mm});
            skCircle(sketch, "E130.2.0", {"center": v(-29.72, -6.78) * mm, "radius": 6 * mm});
            skCircle(sketch, "E130.3.0", {"center": v(-13.22, -27.46) * mm, "radius": 6 * mm});
            skCircle(sketch, "E130.4.0", {"center": v(13.22, -27.46) * mm, "radius": 6 * mm});
            skCircle(sketch, "E130.5.0", {"center": v(29.72, -6.78) * mm, "radius": 6 * mm});
            skCircle(sketch, "E130.6.0", {"center": v(23.83, 19) * mm, "radius": 6 * mm});
            skPoint(sketch, "E130.center", {"position": v(0, 0) * mm});
            skSolve(sketch);
        }
        {
            var Q0;
            Q0=qSketchRegion(id+"F24",true);
            extrude(context, id + "F25", {"entities" : qUnion([Q0]), "operationType" : NewBodyOperationType.REMOVE, "endBound" : BoundingType.THROUGH_ALL, "oppositeDirection" : true, "depth" : 25.4 * mm});
        }
    });
